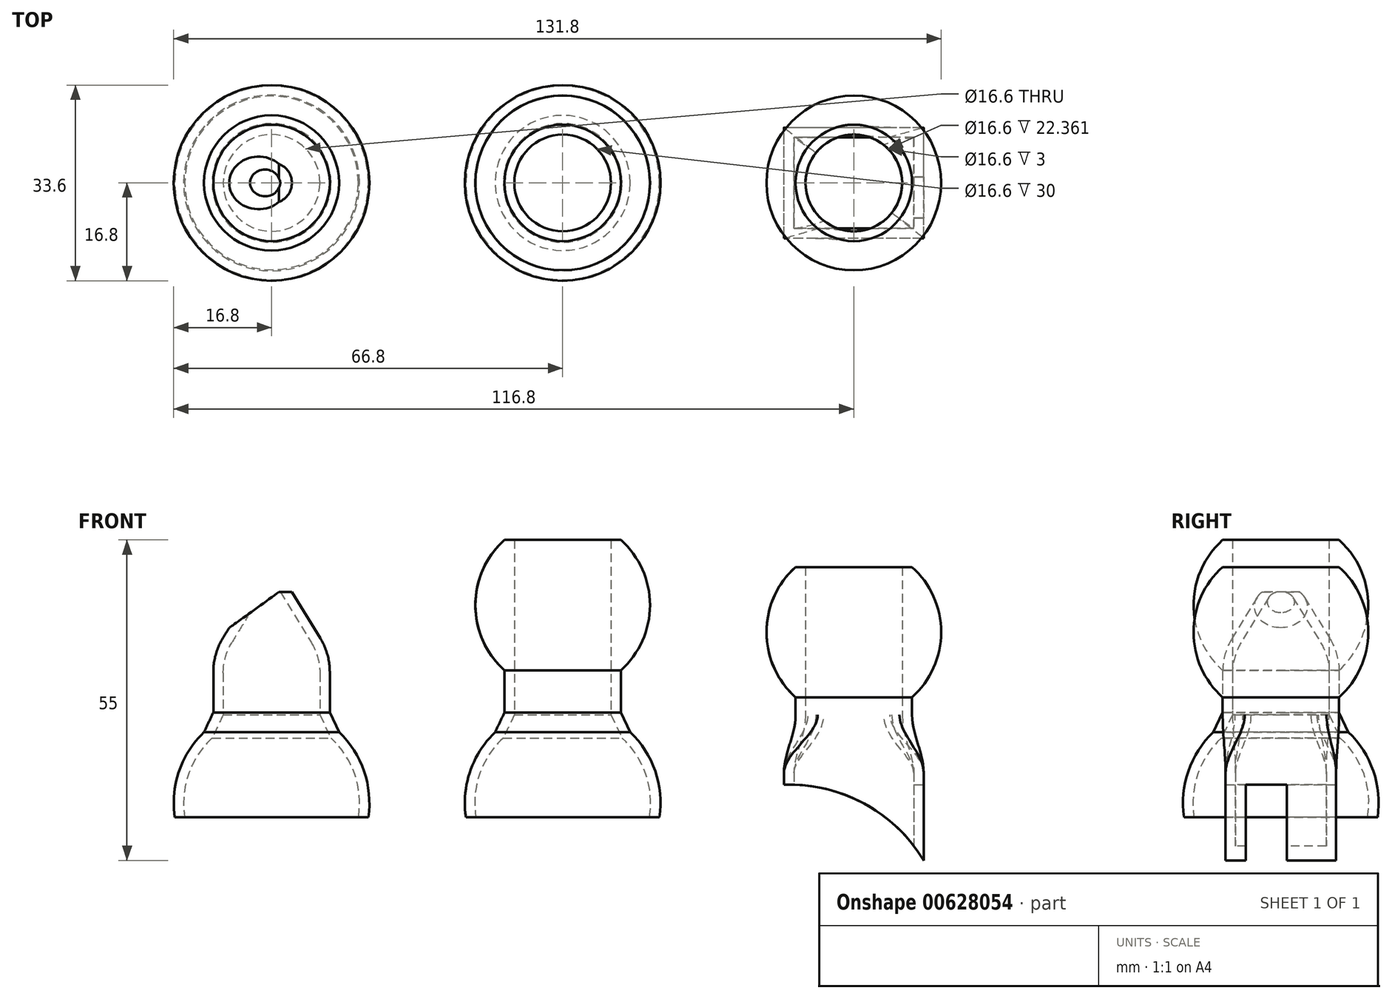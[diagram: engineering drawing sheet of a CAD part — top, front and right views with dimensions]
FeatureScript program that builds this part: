
annotation { "Feature Type Name" : "Feature", "Feature Type Description" : "" }
export const myFeature = defineFeature(function(context is Context, id is Id, definition is map)
    precondition{}
    {
        {
            var Q0;
            Q0=qCreatedBy(makeId("Front.planeOp"),FACE);
            var sketch = newSketch(context, id + "F0", { "sketchPlane" : qUnion([Q0])});
            skLineSegment(sketch, "E0", {"start": v(0, 0) * mm, "end": v(8.3, 0) * mm, "construction": true});
            skLineSegment(sketch, "E1", {"start": v(8.3, 0) * mm, "end": v(8.3, 30) * mm});
            skLineSegment(sketch, "E2", {"start": v(8.3, 30) * mm, "end": v(10, 30) * mm});
            skLineSegment(sketch, "E3", {"start": v(8.3, 30) * mm, "end": v(0, 30) * mm, "construction": true});
            skArc(sketch, "E4", {"start": v(10, 30) * mm, "mid": v(15, 18.82) * mm, "end": v(10, 7.64) * mm});
            skLineSegment(sketch, "E5", {"start": v(0, 30) * mm, "end": v(0, 18.82) * mm, "construction": true});
            skLineSegment(sketch, "E6", {"start": v(0, 0) * mm, "end": v(0, 18.82) * mm, "construction": true});
            skLineSegment(sketch, "E7", {"start": v(8.3, 0) * mm, "end": v(10.2, 0) * mm, "construction": true});
            skLineSegment(sketch, "E8", {"start": v(10.2, 0) * mm, "end": v(10.2, -4) * mm, "construction": true});
            skLineSegment(sketch, "E9", {"start": v(8.3, 0) * mm, "end": v(10.2, -4) * mm});
            skArc(sketch, "E10", {"start": v(10.2, -4) * mm, "mid": v(14.27, -10.2) * mm, "end": v(14.9, -17.58) * mm});
            skLineSegment(sketch, "E11", {"start": v(14.9, -17.58) * mm, "end": v(16.62, -17.58) * mm});
            skArc(sketch, "E12.0", {"start": v(11.6, -2.98) * mm, "mid": v(15.89, -9.67) * mm, "end": v(16.62, -17.58) * mm});
            skLineSegment(sketch, "E12.1", {"start": v(10, 0.38) * mm, "end": v(11.6, -2.98) * mm});
            skLineSegment(sketch, "E13", {"start": v(10, 7.64) * mm, "end": v(10, 0.38) * mm});
            skLineSegment(sketch, "E14", {"start": v(50, 0) * mm, "end": v(58.3, 0) * mm, "construction": true});
            skLineSegment(sketch, "E15", {"start": v(58.3, 0) * mm, "end": v(58.3, 3) * mm});
            skLineSegment(sketch, "E16", {"start": v(58.3, 25.36) * mm, "end": v(60, 25.36) * mm});
            skLineSegment(sketch, "E17", {"start": v(58.3, 25.36) * mm, "end": v(50, 25.36) * mm, "construction": true});
            skArc(sketch, "E18", {"start": v(60, 25.36) * mm, "mid": v(65, 14.18) * mm, "end": v(60, 3) * mm});
            skLineSegment(sketch, "E19", {"start": v(50, 25.36) * mm, "end": v(50, 14.18) * mm, "construction": true});
            skLineSegment(sketch, "E20", {"start": v(50, 0) * mm, "end": v(50, 14.18) * mm, "construction": true});
            skLineSegment(sketch, "E21", {"start": v(60, 3) * mm, "end": v(60, 0) * mm});
            skLineSegment(sketch, "E22", {"start": v(58.3, 0) * mm, "end": v(60, 0) * mm});
            skLineSegment(sketch, "E23", {"start": v(62, -10) * mm, "end": v(38, -10) * mm});
            skLineSegment(sketch, "E24", {"start": v(38, -10) * mm, "end": v(38, -12) * mm});
            skLineSegment(sketch, "E25", {"start": v(62, -10) * mm, "end": v(62, -25) * mm});
            skArc(sketch, "E26", {"start": v(62, -25) * mm, "mid": v(51.76, -15.24) * mm, "end": v(38, -12) * mm});
            skLineSegment(sketch, "E27", {"start": v(60.3, -10) * mm, "end": v(60.3, -22.52) * mm});
            skLineSegment(sketch, "E28", {"start": v(39.7, -10) * mm, "end": v(39.7, -12) * mm});
            skLineSegment(sketch, "E29", {"start": v(60.3, -12) * mm, "end": v(62, -12) * mm});
            skLineSegment(sketch, "E30", {"start": v(60, 3) * mm, "end": v(58.3, 3) * mm});
            skLineSegment(sketch, "E31", {"start": v(58.3, 3) * mm, "end": v(58.3, 3) * mm});
            skLineSegment(sketch, "E32", {"start": v(58.3, 3) * mm, "end": v(58.3, 25.36) * mm});
            skLineSegment(sketch, "E33", {"start": v(58.3, 3) * mm, "end": v(50, 3) * mm});
            skLineSegment(sketch, "E34", {"start": v(50, 3) * mm, "end": v(50, 0) * mm});
            skLineSegment(sketch, "E35", {"start": v(58.3, 0) * mm, "end": v(50, 0) * mm});
            skLineSegment(sketch, "E36", {"start": v(50, 0) * mm, "end": v(50, 3) * mm});
            skLineSegment(sketch, "E37", {"start": v(60.3, -12) * mm, "end": v(38, -12) * mm});
            skLineSegment(sketch, "E38", {"start": v(-50, 0) * mm, "end": v(-41.7, 0) * mm, "construction": true});
            skLineSegment(sketch, "E39", {"start": v(-41.7, 0) * mm, "end": v(-41.7, 7.18) * mm});
            skLineSegment(sketch, "E40", {"start": v(-41.7, 10) * mm, "end": v(-50, 10) * mm, "construction": true});
            skLineSegment(sketch, "E41", {"start": v(-50, 27) * mm, "end": v(-50, 10) * mm, "construction": true});
            skLineSegment(sketch, "E42", {"start": v(-50, 0) * mm, "end": v(-50, 27) * mm, "construction": true});
            skLineSegment(sketch, "E43", {"start": v(-41.7, 0) * mm, "end": v(-39.8, 0) * mm, "construction": true});
            skLineSegment(sketch, "E44", {"start": v(-39.8, 0) * mm, "end": v(-39.8, -4) * mm, "construction": true});
            skLineSegment(sketch, "E45", {"start": v(-41.7, 0) * mm, "end": v(-39.8, -4) * mm});
            skArc(sketch, "E46", {"start": v(-39.8, -4) * mm, "mid": v(-35.73, -10.2) * mm, "end": v(-35.1, -17.58) * mm});
            skLineSegment(sketch, "E47", {"start": v(-35.1, -17.58) * mm, "end": v(-33.38, -17.58) * mm});
            skArc(sketch, "E48.0", {"start": v(-38.4, -2.98) * mm, "mid": v(-34.11, -9.67) * mm, "end": v(-33.38, -17.58) * mm});
            skLineSegment(sketch, "E48.1", {"start": v(-40, 0.38) * mm, "end": v(-38.4, -2.98) * mm});
            skLineSegment(sketch, "E49", {"start": v(-40, 7.37) * mm, "end": v(-40, 0.38) * mm});
            skLineSegment(sketch, "E50", {"start": v(-43.18, 12.4) * mm, "end": v(-48.5, 21.08) * mm});
            skLineSegment(sketch, "E51", {"start": v(-48.5, 21.08) * mm, "end": v(-46.5, 21.08) * mm});
            skLineSegment(sketch, "E52.0", {"start": v(-41.62, 13.13) * mm, "end": v(-46.5, 21.08) * mm});
            skPoint(sketch, "E53.visualSharp", {"position": v(-41.7, 10) * mm});
            skArc(sketch, "E53.filletArc", {"start": v(-41.7, 7.18) * mm, "mid": v(-42.08, 9.9) * mm, "end": v(-43.18, 12.4) * mm});
            skPoint(sketch, "E54.visualSharp", {"position": v(-40, 10.48) * mm});
            skArc(sketch, "E54.filletArc", {"start": v(-40, 7.37) * mm, "mid": v(-40.41, 10.36) * mm, "end": v(-41.62, 13.13) * mm});
            skLineSegment(sketch, "E55", {"start": v(-46.05, 22.99) * mm, "end": v(-58.92, 13.75) * mm});
            skLineSegment(sketch, "E56", {"start": v(-58.92, 13.75) * mm, "end": v(-61.69, 17.6) * mm});
            skLineSegment(sketch, "E57", {"start": v(-61.69, 17.6) * mm, "end": v(-48.44, 27.12) * mm});
            skLineSegment(sketch, "E58", {"start": v(-48.44, 27.12) * mm, "end": v(-46.05, 22.99) * mm});
            skSolve(sketch);
        }
        {
            var Q0;
            Q0=makeQuery(id+"F0.imprint","IMPRINT",FACE,{"disambiguationData":[TD([[makeQuery(id+"F0.imprint","IMPRINT",EDGE,{"derivedFrom":sQuery(id+"F0.wireOp",EDGE,"E1")}),-1.0]])]});
            var Q1;
            Q1=sQuery(id+"F0.wireOp",EDGE,"E6");
            revolve(context, id + "F1", {"entities" : qUnion([Q0]), "axis" : qUnion([Q1]), "revolveType" : RevolveType.FULL});
        }
        {
            var Q0;
            Q0=makeQuery(id+"F0.imprint","IMPRINT",FACE,{"disambiguationData":[TD([[makeQuery(id+"F0.imprint","IMPRINT",EDGE,{"derivedFrom":sQuery(id+"F0.wireOp",EDGE,"E16")}),-1.0]])]});
            var Q1;
            Q1=sQuery(id+"F0.wireOp",EDGE,"E20");
            revolve(context, id + "F2", {"entities" : qUnion([Q0]), "axis" : qUnion([Q1]), "revolveType" : RevolveType.FULL});
        }
        {
            var Q0;
            {var subQ0=sQuery(id+"F0.wireOp",EDGE,"E24");Q0=makeQuery(id+"F0.imprint","IMPRINT",FACE,{"disambiguationData":[TD([[makeQuery(id+"F0.imprint","IMPRINT",EDGE,{"derivedFrom":subQ0}),1.0]])]});}
            var Q1;
            {var subQ0=sQuery(id+"F0.wireOp",EDGE,"E27");Q1=makeQuery(id+"F0.imprint","IMPRINT",FACE,{"disambiguationData":[TD([[makeQuery(id+"F0.imprint","IMPRINT",EDGE,{"derivedFrom":subQ0}),-1.0]])]});}
            var Q2;
            {var subQ0=sQuery(id+"F0.wireOp",EDGE,"E25");Q2=makeQuery(id+"F0.imprint","IMPRINT",FACE,{"disambiguationData":[TD([[makeQuery(id+"F0.imprint","IMPRINT",EDGE,{"derivedFrom":subQ0}),-1.0]])]});}
            var Q3;
            {var subQ0=sQuery(id+"F0.wireOp",EDGE,"E28");Q3=makeQuery(id+"F0.imprint","IMPRINT",FACE,{"disambiguationData":[TD([[makeQuery(id+"F0.imprint","IMPRINT",EDGE,{"derivedFrom":subQ0}),1.0]])]});}
            extrude(context, id + "F3", {"entities" : qUnion([Q0, Q1, Q2, Q3]), "depth" : 9.5 * mm, "offsetDistance" : 25 * mm, "hasSecondDirection" : true, "secondDirectionOppositeDirection" : true, "secondDirectionDepth" : 9.5 * mm});
        }
        {
            var Q0;
            {var subQ0=sQuery(id+"F0.wireOp",EDGE,"E27");Q0=makeQuery(id+"F0.imprint","IMPRINT",FACE,{"disambiguationData":[TD([[makeQuery(id+"F0.imprint","IMPRINT",EDGE,{"derivedFrom":subQ0}),-1.0]])]});}
            extrude(context, id + "F4", {"entities" : qUnion([Q0]), "operationType" : NewBodyOperationType.REMOVE, "oppositeDirection" : true, "depth" : 7.8 * mm, "offsetDistance" : 25 * mm, "hasSecondDirection" : true, "secondDirectionOppositeDirection" : false, "secondDirectionDepth" : 7.8 * mm});
        }
        {
            var Q0;
            {var subQ3=sQuery(id+"F0.wireOp",EDGE,"E29");Q0=makeQuery(id+"F0.imprint","IMPRINT",FACE,{"disambiguationData":[TD([[makeQuery(id+"F0.imprint","IMPRINT",EDGE,{"derivedFrom":subQ3}),-1.0]])]});}
            extrude(context, id + "F5", {"entities" : qUnion([Q0]), "operationType" : NewBodyOperationType.REMOVE, "oppositeDirection" : true, "depth" : 1 * mm, "offsetDistance" : 25 * mm, "hasSecondDirection" : true, "secondDirectionOppositeDirection" : false, "secondDirectionDepth" : 6 * mm});
        }
        {
            var Q0;
            Q0=makeQuery(id+"F0.imprint","IMPRINT",FACE,{"disambiguationData":[TD([[makeQuery(id+"F0.imprint","IMPRINT",EDGE,{"derivedFrom":sQuery(id+"F0.wireOp",EDGE,"E15")}),-1.0]])]});
            var Q1;
            Q1=makeQuery(id+"F0.imprint","IMPRINT",FACE,{"disambiguationData":[TD([[makeQuery(id+"F0.imprint","IMPRINT",EDGE,{"derivedFrom":sQuery(id+"F0.wireOp",EDGE,"E15")}),1.0]])]});
            var Q2;
            Q2=sQuery(id+"F0.wireOp",EDGE,"E20");
            revolve(context, id + "F6", {"entities" : qUnion([Q0, Q1]), "axis" : qUnion([Q2]), "revolveType" : RevolveType.FULL});
        }
        {
            var Q2;
            Q2=makeQuery(id+"F3.opExtrude","SWEPT_FACE",FACE,{"disambiguationData":[OSD([sQuery(id+"F0.wireOp",EDGE,"E23")])]});
            var Q3;
            Q3=makeQuery(id+"F6.opRevolve","SWEPT_FACE",FACE,{"disambiguationData":[OSD([sQuery(id+"F0.wireOp",EDGE,"E22"),sQuery(id+"F0.wireOp",EDGE,"E35")])]});
            loft(context, id + "F7", {"operationType" : NewBodyOperationType.ADD, "startCondition" : LoftEndDerivativeType.MATCH_TANGENT, "startMagnitude" : 1, "endCondition" : LoftEndDerivativeType.MATCH_TANGENT, "endMagnitude" : 1, "sheetProfilesArray" : [{ "sheetProfileEntities" : qUnion([Q2]) }, { "sheetProfileEntities" : qUnion([Q3]) }]});
        }
        {
            var Q0;
            Q0=makeQuery(id+"F6.opRevolve","SWEPT_FACE",FACE,{"disambiguationData":[OSD([sQuery(id+"F0.wireOp",EDGE,"E30"),sQuery(id+"F0.wireOp",EDGE,"E33")])]});
            shell(context, id + "F8", {"entities" : qUnion([Q0]), "thickness" : 1.7 * mm});
        }
        {
            var Q0;
            {var subQ0=sQuery(id+"F0.wireOp",EDGE,"E28");Q0=makeQuery(id+"F0.imprint","IMPRINT",FACE,{"disambiguationData":[TD([[makeQuery(id+"F0.imprint","IMPRINT",EDGE,{"derivedFrom":subQ0}),1.0]])]});}
            extrude(context, id + "F9", {"entities" : qUnion([Q0]), "operationType" : NewBodyOperationType.REMOVE, "oppositeDirection" : true, "depth" : 7.8 * mm, "offsetDistance" : 25 * mm, "hasSecondDirection" : true, "secondDirectionOppositeDirection" : false, "secondDirectionDepth" : 7.8 * mm});
        }
        {
            var Q0;
            Q0=makeQuery(id+"F0.imprint","IMPRINT",FACE,{"disambiguationData":[TD([[makeQuery(id+"F0.imprint","IMPRINT",EDGE,{"derivedFrom":sQuery(id+"F0.wireOp",EDGE,"E39")}),-1.0]])]});
            var Q1;
            Q1=sQuery(id+"F0.wireOp",EDGE,"E42");
            revolve(context, id + "F10", {"entities" : qUnion([Q0]), "axis" : qUnion([Q1]), "revolveType" : RevolveType.FULL});
        }
        {
            var Q0;
            Q0=makeQuery(id+"F0.imprint","IMPRINT",FACE,{"disambiguationData":[TD([[makeQuery(id+"F0.imprint","IMPRINT",EDGE,{"derivedFrom":sQuery(id+"F0.wireOp",EDGE,"E55")}),-1.0]])]});
            extrude(context, id + "F11", {"entities" : qUnion([Q0]), "operationType" : NewBodyOperationType.REMOVE, "oppositeDirection" : true, "depth" : 25 * mm, "offsetDistance" : 25 * mm, "hasSecondDirection" : true, "secondDirectionOppositeDirection" : false, "secondDirectionDepth" : 25 * mm});
        }
    });
